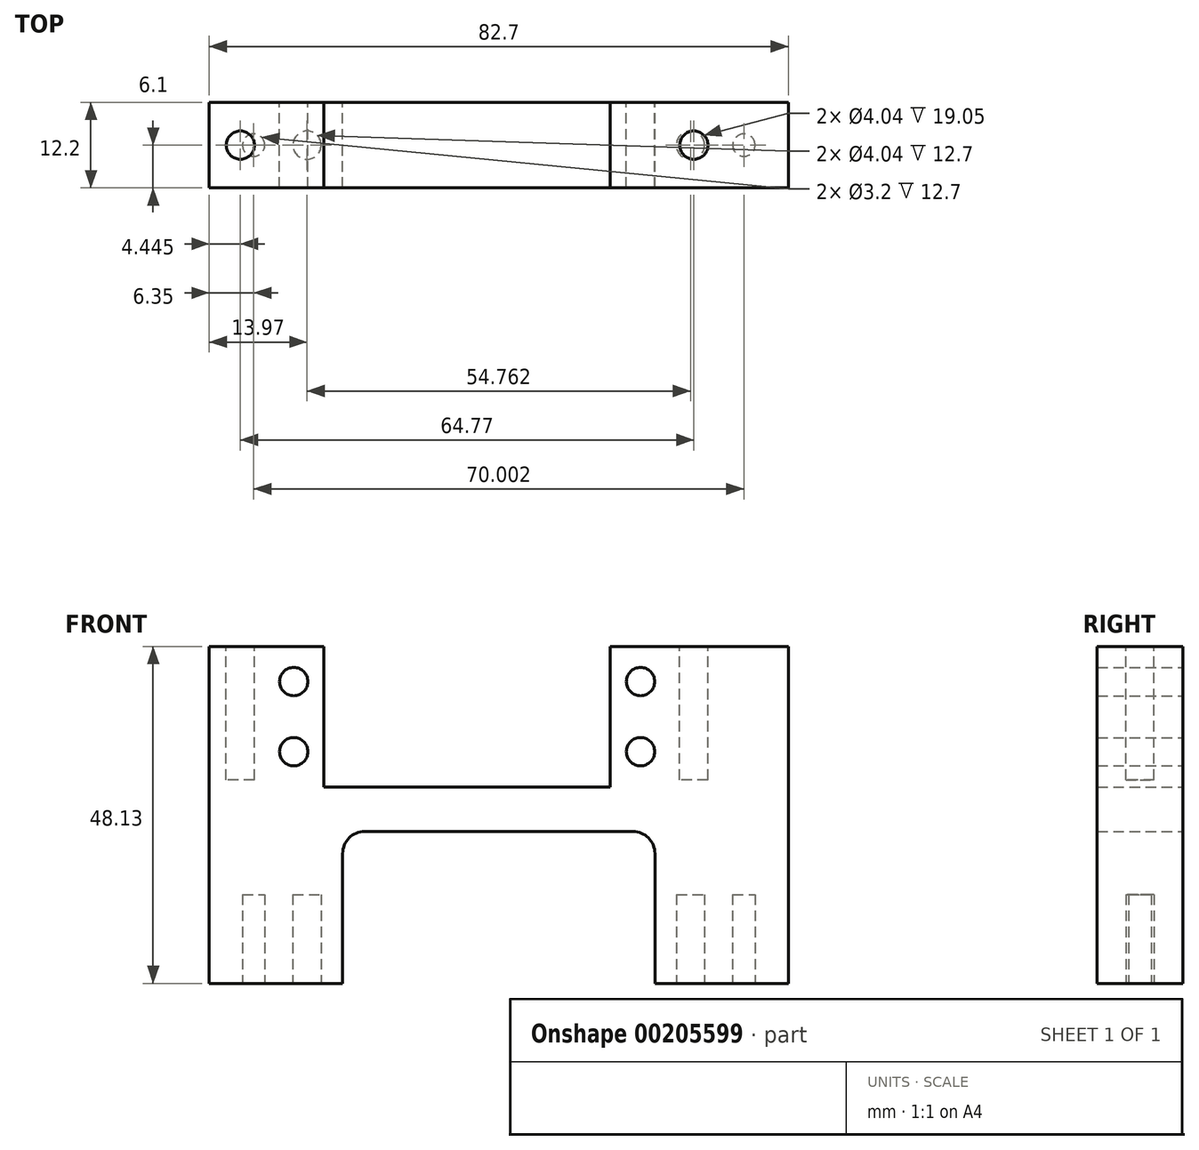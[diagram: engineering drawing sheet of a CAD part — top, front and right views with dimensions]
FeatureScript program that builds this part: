
annotation { "Feature Type Name" : "Feature", "Feature Type Description" : "" }
export const myFeature = defineFeature(function(context is Context, id is Id, definition is map)
    precondition{}
    {
        {
            var Q0;
            Q0=qCreatedBy(makeId("Front.planeOp"),FACE);
            var sketch = newSketch(context, id + "F0", { "sketchPlane" : qUnion([Q0])});
            skLineSegment(sketch, "E0", {"start": v(-36.83, 0) * mm, "end": v(-17.78, 0) * mm});
            skLineSegment(sketch, "E1", {"start": v(45.87, 0) * mm, "end": v(45.87, 48.13) * mm});
            skLineSegment(sketch, "E2", {"start": v(45.87, 48.13) * mm, "end": v(20.45, 48.13) * mm});
            skLineSegment(sketch, "E3", {"start": v(20.45, 48.13) * mm, "end": v(20.45, 28.07) * mm});
            skLineSegment(sketch, "E4", {"start": v(20.45, 28.07) * mm, "end": v(-20.45, 28.07) * mm});
            skLineSegment(sketch, "E5", {"start": v(-20.45, 28.07) * mm, "end": v(-20.45, 48.13) * mm});
            skLineSegment(sketch, "E6", {"start": v(-20.45, 48.13) * mm, "end": v(-36.83, 48.13) * mm});
            skLineSegment(sketch, "E7", {"start": v(-36.83, 48.13) * mm, "end": v(-36.83, 0) * mm});
            skCircle(sketch, "E8", {"center": v(-24.77, 43.1) * mm, "radius": 2.02 * mm});
            skCircle(sketch, "E9", {"center": v(-24.77, 33.1) * mm, "radius": 2.02 * mm});
            skCircle(sketch, "E10", {"center": v(24.77, 43.1) * mm, "radius": 2.02 * mm});
            skCircle(sketch, "E11", {"center": v(24.77, 33.1) * mm, "radius": 2.02 * mm});
            skLineSegment(sketch, "E12", {"start": v(-17.78, 0) * mm, "end": v(-17.78, 21.72) * mm});
            skLineSegment(sketch, "E13", {"start": v(-17.78, 21.72) * mm, "end": v(26.82, 21.72) * mm});
            skLineSegment(sketch, "E14", {"start": v(26.82, 21.72) * mm, "end": v(26.82, 0) * mm});
            skLineSegment(sketch, "E15.trimOffspring", {"start": v(26.82, 0) * mm, "end": v(45.87, 0) * mm});
            skSolve(sketch);
        }
        {
            var Q0;
            Q0=qSketchRegion(id+"F0",true);
            extrude(context, id + "F1", {"entities" : qUnion([Q0]), "depth" : 12.2 * mm, "symmetric" : true});
        }
        {
            var Q0;
            Q0=makeQuery(id+"F1.opExtrude","SWEPT_FACE",FACE,{"disambiguationData":[OSD([sQuery(id+"F0.wireOp",EDGE,"E6")])]});
            var sketch = newSketch(context, id + "F2", { "sketchPlane" : qUnion([Q0])});
            skCircle(sketch, "E16", {"center": v(-32.38, 0) * mm, "radius": 2.02 * mm});
            skCircle(sketch, "E17", {"center": v(32.39, 0) * mm, "radius": 2.02 * mm});
            skSolve(sketch);
        }
        {
            var Q0;
            Q0=qSketchRegion(id+"F2",true);
            extrude(context, id + "F3", {"entities" : qUnion([Q0]), "operationType" : NewBodyOperationType.REMOVE, "oppositeDirection" : true, "depth" : 19.05 * mm});
        }
        {
            var Q0;
            Q0=makeQuery(id+"F1.opExtrude","SWEPT_FACE",FACE,{"disambiguationData":[OSD([sQuery(id+"F0.wireOp",EDGE,"E0")])]});
            var sketch = newSketch(context, id + "F4", { "sketchPlane" : qUnion([Q0])});
            skCircle(sketch, "E18", {"center": v(39.52, 0) * mm, "radius": 1.6 * mm});
            skCircle(sketch, "E19", {"center": v(31.9, 0) * mm, "radius": 2.02 * mm});
            skCircle(sketch, "E20", {"center": v(-22.86, 0) * mm, "radius": 2.02 * mm});
            skCircle(sketch, "E21", {"center": v(-30.48, 0) * mm, "radius": 1.6 * mm});
            skSolve(sketch);
        }
        {
            var Q0;
            Q0=qSketchRegion(id+"F4",true);
            extrude(context, id + "F5", {"entities" : qUnion([Q0]), "operationType" : NewBodyOperationType.REMOVE, "oppositeDirection" : true, "depth" : 12.7 * mm});
        }
        {
            var Q0;
            Q0=makeQuery(id+"F1.opExtrude","SWEPT_EDGE",EDGE,{"disambiguationData":[OSD([sQuery(id+"F0.wireOp",EDGE,"E12"),sQuery(id+"F0.wireOp",EDGE,"E13")])]});
            var Q1;
            Q1=makeQuery(id+"F1.opExtrude","SWEPT_EDGE",EDGE,{"disambiguationData":[OSD([sQuery(id+"F0.wireOp",EDGE,"E13"),sQuery(id+"F0.wireOp",EDGE,"E14")])]});
            fillet(context, id + "F6", {"entities" : qUnion([Q0, Q1]), "radius" : 3.17 * mm, "tangentPropagation" : true, "allowEdgeOverflow" : false});
        }
    });
